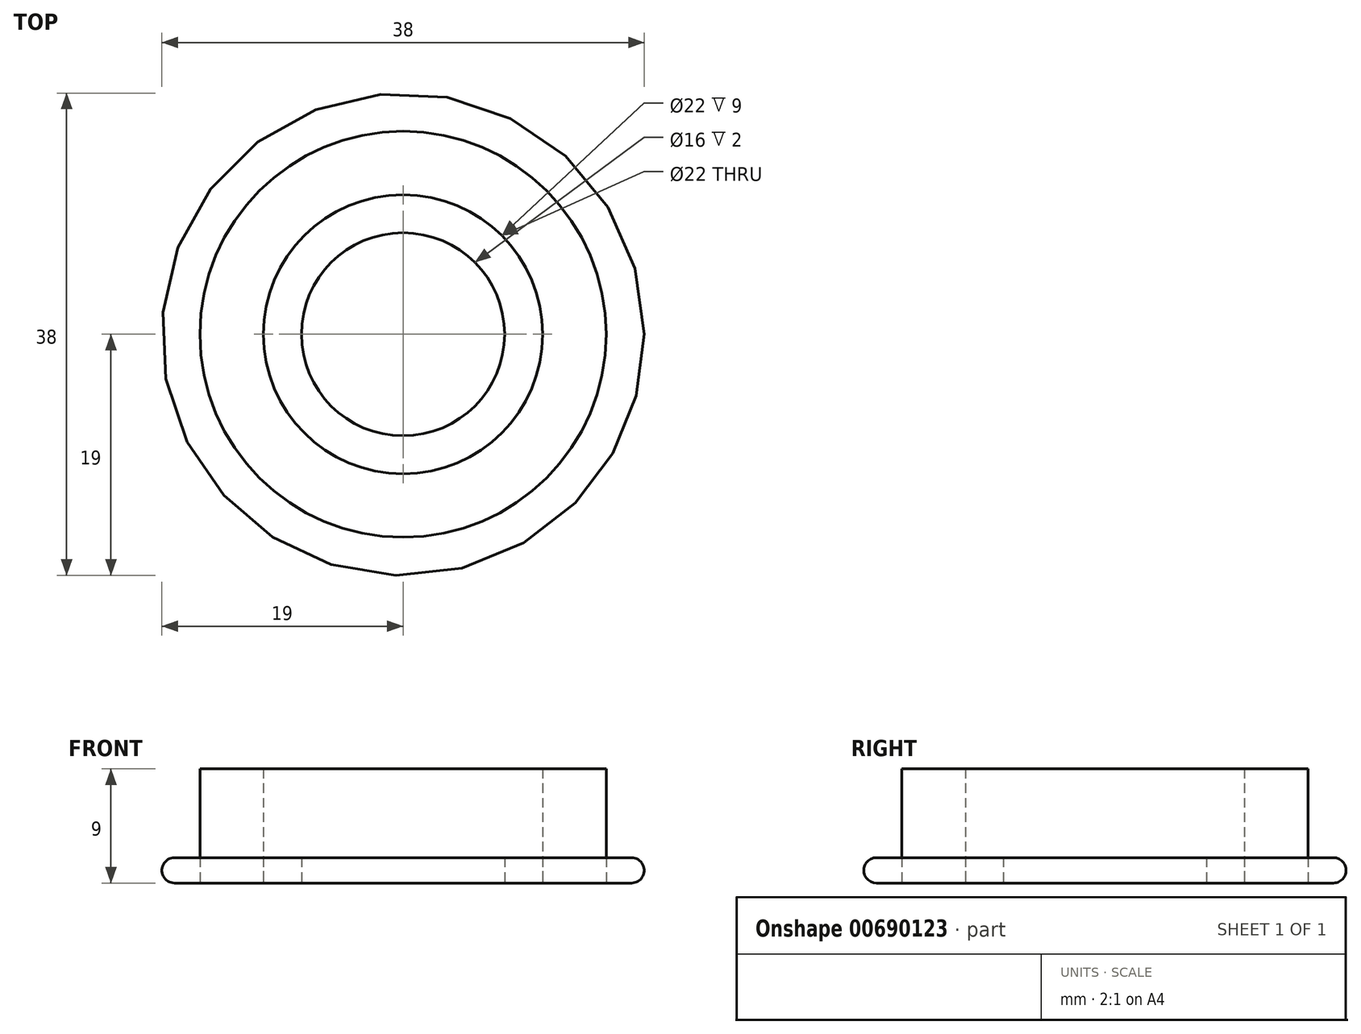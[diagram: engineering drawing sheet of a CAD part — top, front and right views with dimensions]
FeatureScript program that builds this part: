
annotation { "Feature Type Name" : "Feature", "Feature Type Description" : "" }
export const myFeature = defineFeature(function(context is Context, id is Id, definition is map)
    precondition{}
    {
        {
            var Q0;
            Q0=qCreatedBy(makeId("Top.planeOp"),FACE);
            var sketch = newSketch(context, id + "F0", { "sketchPlane" : qUnion([Q0])});
            skCircle(sketch, "E0", {"center": v(0, 0) * mm, "radius": 11 * mm});
            skCircle(sketch, "E1", {"center": v(0, 0) * mm, "radius": 16 * mm});
            skCircle(sketch, "E2", {"center": v(0, 0) * mm, "radius": 19 * mm});
            skCircle(sketch, "E3", {"center": v(0, 0) * mm, "radius": 8 * mm});
            skSolve(sketch);
        }
        {
            var Q0;
            Q0=makeQuery(id+"F0.imprint","IMPRINT",FACE,{"disambiguationData":[TD([[makeQuery(id+"F0.imprint","IMPRINT",EDGE,{"derivedFrom":sQuery(id+"F0.wireOp",EDGE,"E1")}),-1.0]])]});
            var Q1;
            Q1=makeQuery(id+"F0.imprint","IMPRINT",FACE,{"disambiguationData":[TD([[makeQuery(id+"F0.imprint","IMPRINT",EDGE,{"derivedFrom":sQuery(id+"F0.wireOp",EDGE,"E0")}),-1.0]])]});
            extrude(context, id + "F1", {"entities" : qUnion([Q0, Q1]), "depth" : 2 * mm, "offsetDistance" : 25 * mm});
        }
        {
            var Q0;
            Q0=makeQuery(id+"F0.imprint","IMPRINT",FACE,{"disambiguationData":[TD([[makeQuery(id+"F0.imprint","IMPRINT",EDGE,{"derivedFrom":sQuery(id+"F0.wireOp",EDGE,"E0")}),-1.0]])]});
            extrude(context, id + "F2", {"entities" : qUnion([Q0]), "depth" : 9 * mm, "offsetDistance" : 25 * mm});
        }
        {
            var Q0;
            Q0=makeQuery(id+"F1.opExtrude","CAP_EDGE",EDGE,{"disambiguationData":[OSD([sQuery(id+"F0.wireOp",EDGE,"E2")])],"isStart":false});
            fillet(context, id + "F3", {"entities" : qUnion([Q0]), "radius" : 1 * mm, "tangentPropagation" : true, "allowEdgeOverflow" : false});
        }
        {
            var Q0;
            Q0=makeQuery(id+"F1.opExtrude","CAP_EDGE",EDGE,{"disambiguationData":[OSD([sQuery(id+"F0.wireOp",EDGE,"E2")])],"isStart":true});
            fillet(context, id + "F4", {"entities" : qUnion([Q0]), "radius" : 1 * mm, "tangentPropagation" : true, "allowEdgeOverflow" : false});
        }
        {
            var Q0;
            Q0=makeQuery(id+"F0.imprint","IMPRINT",FACE,{"disambiguationData":[TD([[makeQuery(id+"F0.imprint","IMPRINT",EDGE,{"derivedFrom":sQuery(id+"F0.wireOp",EDGE,"E0")}),1.0]])]});
            extrude(context, id + "F5", {"entities" : qUnion([Q0]), "depth" : 2 * mm, "offsetDistance" : 25 * mm});
        }
    });
